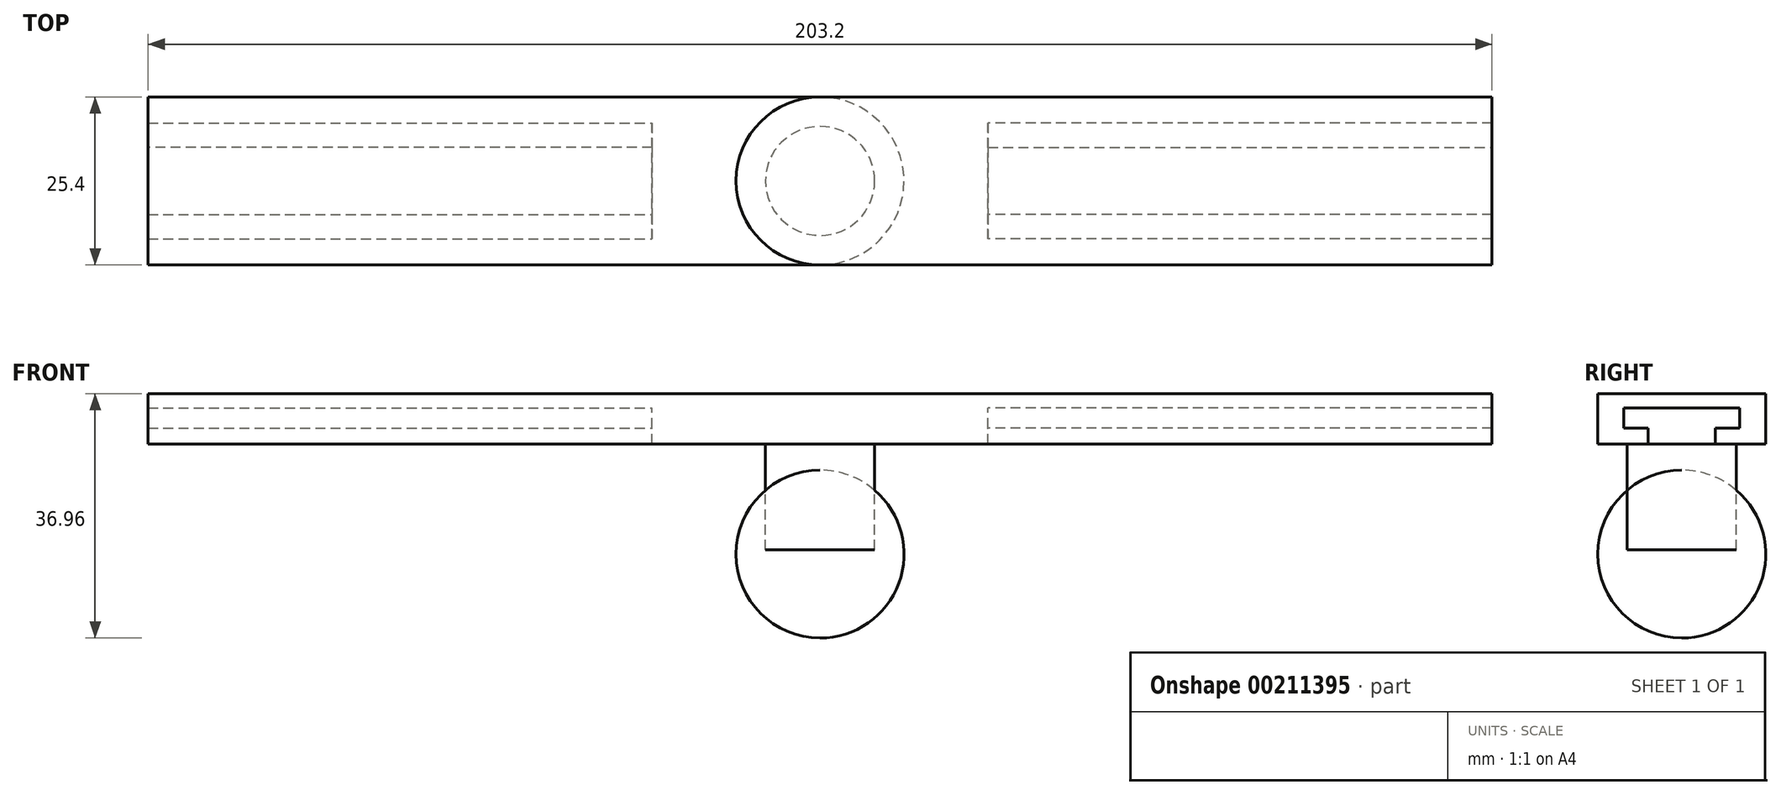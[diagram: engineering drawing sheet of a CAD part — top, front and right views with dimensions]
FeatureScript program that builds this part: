
annotation { "Feature Type Name" : "Feature", "Feature Type Description" : "" }
export const myFeature = defineFeature(function(context is Context, id is Id, definition is map)
    precondition{}
    {
        {
            var Q0;
            Q0=qCreatedBy(makeId("Right.planeOp"),FACE);
            var sketch = newSketch(context, id + "F0", { "sketchPlane" : qUnion([Q0])});
            skLineSegment(sketch, "E0.bottom", {"start": v(12.7, -3.8) * mm, "end": v(-12.7, -3.8) * mm});
            skLineSegment(sketch, "E0.top", {"start": v(12.7, 3.81) * mm, "end": v(-12.7, 3.81) * mm});
            skLineSegment(sketch, "E0.left", {"start": v(12.7, -3.8) * mm, "end": v(12.7, 3.81) * mm});
            skLineSegment(sketch, "E0.right", {"start": v(-12.7, -3.8) * mm, "end": v(-12.7, 3.81) * mm});
            skPoint(sketch, "E0.middle", {"position": v(0, 0) * mm});
            skSolve(sketch);
        }
        {
            var Q0;
            Q0 = qSketchRegion(id + "F0", true);
            extrude(context, id + "F1", {"entities" : qUnion([Q0]), "endBound" : BoundingType.SYMMETRIC, "depth" : 203.2 * mm});
        }
        {
            var Q0;
            Q0=qCreatedBy(makeId("Right.planeOp"),FACE);
            var sketch = newSketch(context, id + "F2", { "sketchPlane" : qUnion([Q0])});
            skLineSegment(sketch, "E1", {"start": v(-8.76, 1.68) * mm, "end": v(8.76, 1.68) * mm});
            skLineSegment(sketch, "E2", {"start": v(8.76, 1.68) * mm, "end": v(8.76, -1.37) * mm});
            skLineSegment(sketch, "E3", {"start": v(8.76, -1.37) * mm, "end": v(5.08, -1.37) * mm});
            skLineSegment(sketch, "E4", {"start": v(5.08, -1.37) * mm, "end": v(5.08, -3.83) * mm});
            skLineSegment(sketch, "E5", {"start": v(5.08, -3.83) * mm, "end": v(-5.08, -3.83) * mm});
            skLineSegment(sketch, "E6", {"start": v(-5.08, -3.83) * mm, "end": v(-5.08, -1.37) * mm});
            skLineSegment(sketch, "E7", {"start": v(-5.08, -1.37) * mm, "end": v(-8.76, -1.37) * mm});
            skLineSegment(sketch, "E8", {"start": v(-8.76, -1.37) * mm, "end": v(-8.76, 1.68) * mm});
            skLineSegment(sketch, "E9.bottom", {"start": v(12.7, 3.81) * mm, "end": v(-12.7, 3.81) * mm, "construction": true});
            skLineSegment(sketch, "E9.top", {"start": v(12.7, -3.81) * mm, "end": v(-12.7, -3.81) * mm, "construction": true});
            skLineSegment(sketch, "E9.left", {"start": v(12.7, 3.81) * mm, "end": v(12.7, -3.81) * mm, "construction": true});
            skLineSegment(sketch, "E9.right", {"start": v(-12.7, 3.81) * mm, "end": v(-12.7, -3.81) * mm, "construction": true});
            skPoint(sketch, "E9.middle", {"position": v(0, 0) * mm});
            skLineSegment(sketch, "E10", {"start": v(-12.7, 3.81) * mm, "end": v(-8.76, 1.68) * mm, "construction": true});
            skLineSegment(sketch, "E11", {"start": v(8.76, 1.68) * mm, "end": v(12.7, 3.81) * mm, "construction": true});
            skLineSegment(sketch, "E12", {"start": v(8.76, -1.37) * mm, "end": v(12.7, -3.81) * mm, "construction": true});
            skLineSegment(sketch, "E13", {"start": v(-12.7, -3.8) * mm, "end": v(-8.76, -1.37) * mm, "construction": true});
            skLineSegment(sketch, "E14", {"start": v(-5.08, -1.37) * mm, "end": v(5.08, -1.37) * mm, "construction": true});
            skSolve(sketch);
        }
        {
            var Q0;
            Q0 = qSketchRegion(id + "F2", true);
            var Q1;
            Q1=makeQuery(id+"F1.opExtrude","CAP_FACE",FACE,{"disambiguationData":[OSD([sQuery(id+"F0.wireOp",EDGE,"E0.bottom"),sQuery(id+"F0.wireOp",EDGE,"E0.top"),sQuery(id+"F0.wireOp",EDGE,"E0.left"),sQuery(id+"F0.wireOp",EDGE,"E0.right")])],"isStart":true});
            extrude(context, id + "F3", {"entities" : qUnion([Q0]), "operationType" : NewBodyOperationType.REMOVE, "oppositeDirection" : true, "endBoundEntityFace" : qUnion([Q1]), "depth" : 119.13 * mm, "hasSecondDirection" : true, "secondDirectionOppositeDirection" : true, "secondDirectionDepth" : 25.4 * mm});
        }
        {
            var Q0;
            Q0 = qSketchRegion(id + "F2", true);
            extrude(context, id + "F4", {"entities" : qUnion([Q0]), "operationType" : NewBodyOperationType.REMOVE, "depth" : 127 * mm, "hasSecondDirection" : true, "secondDirectionOppositeDirection" : false, "secondDirectionDepth" : 25.4 * mm});
        }
        {
            var Q0;
            Q0=makeQuery(id+"F1.opExtrude","SWEPT_FACE",FACE,{"disambiguationData":[OSD([sQuery(id+"F0.wireOp",EDGE,"E0.bottom")])]});
            var sketch = newSketch(context, id + "F5", { "sketchPlane" : qUnion([Q0])});
            skCircle(sketch, "E15", {"center": v(0, 0) * mm, "radius": 8.26 * mm});
            skSolve(sketch);
        }
        {
            var Q0;
            Q0 = qSketchRegion(id + "F5", true);
            extrude(context, id + "F6", {"entities" : qUnion([Q0]), "operationType" : NewBodyOperationType.ADD, "depth" : 16 * mm});
        }
        {
            var Q0;
            Q0=qCreatedBy(makeId("Front.planeOp"),FACE);
            var sketch = newSketch(context, id + "F7", { "sketchPlane" : qUnion([Q0])});
            skArc(sketch, "E16", {"start": v(0, -33.15) * mm, "mid": v(12.7, -20.45) * mm, "end": v(0, -7.75) * mm});
            skLineSegment(sketch, "E17", {"start": v(0, -7.75) * mm, "end": v(0, -20.45) * mm});
            skLineSegment(sketch, "E18", {"start": v(0, -20.45) * mm, "end": v(0, -33.15) * mm});
            skSolve(sketch);
        }
        {
            var Q0;
            Q0 = qSketchRegion(id + "F7", true);
            var Q1;
            Q1=sQuery(id+"F7.wireOp",EDGE,"E18");
            revolve(context, id + "F8", {"entities" : qUnion([Q0]), "axis" : qUnion([Q1]), "revolveType" : RevolveType.FULL});
        }
    });
